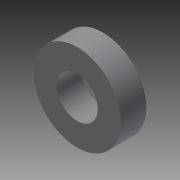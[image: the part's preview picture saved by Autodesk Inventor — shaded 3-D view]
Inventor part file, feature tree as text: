
AUTODESK INVENTOR PART (.ipt)
format: ipt  version: 2014 SP2 (Build 180246200, 246)  size: 95,744 bytes
history: native  units: in
note: dims shown in document units (in); Inventor stores cm internally (conversion verified against a paired STEP export)
features: other x7, revolve x1, sketch x1
ambient origin geometry x8: Origin, YZ Plane, XZ Plane, XY Plane, X Axis, Y Axis, Z Axis, Center Point
bodies: Solid1 (feature_tree)
feature tree (9):
  revolve  "Revolution1"  [1 undecoded]
  other  "part_to_rod_XY"
  other  "part_to_rod_YZ"
  other  "part_to_rod_ZX"
  other  "part_to_rod_X"
  other  "part_to_rod_Y"
  other  "part_to_rod_Z"
  other  "part_to_rod_Center"
  sketch  "Sketch_1"  dims[d0=360.0deg]
note: 1 required parameter value undecoded (feature->parameter linkage not recoverable at this tier; creation-order binding heuristic only, values carry confidence <= 0.55)
